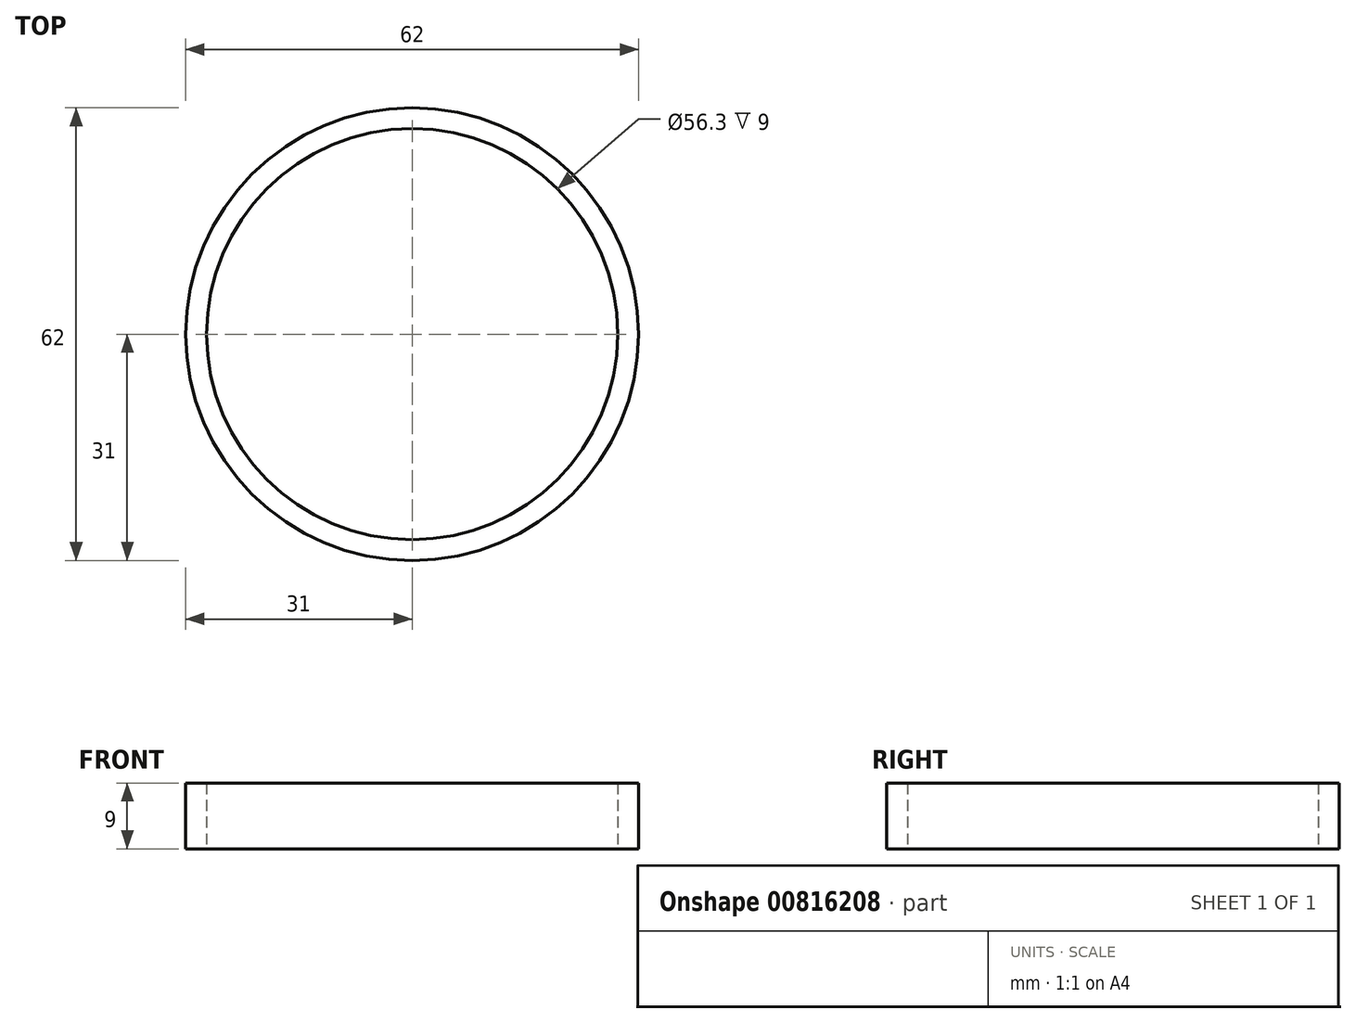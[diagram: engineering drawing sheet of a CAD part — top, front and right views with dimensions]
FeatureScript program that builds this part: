
annotation { "Feature Type Name" : "Feature", "Feature Type Description" : "" }
export const myFeature = defineFeature(function(context is Context, id is Id, definition is map)
    precondition{}
    {
        {
            var Q0;
            Q0=qCreatedBy(makeId("Top.planeOp"),FACE);
            var sketch = newSketch(context, id + "F0", { "sketchPlane" : qUnion([Q0])});
            skCircle(sketch, "E0", {"center": v(0, 0) * mm, "radius": 31 * mm});
            skCircle(sketch, "E1", {"center": v(0, 0) * mm, "radius": 28.15 * mm});
            skSolve(sketch);
        }
        {
            var Q0;
            Q0=makeQuery(id+"F0.imprint","IMPRINT",FACE,{"disambiguationData":[TD([[makeQuery(id+"F0.imprint","IMPRINT",EDGE,{"derivedFrom":sQuery(id+"F0.wireOp",EDGE,"E0")}),1.0]])]});
            var Q1;
            Q1=sQuery(id+"F0.wireOp",EDGE,"E0");
            extrude(context, id + "F1", {"entities" : qUnion([Q0]), "surfaceEntities" : qUnion([Q1]), "depth" : 9 * mm, "offsetDistance" : 25 * mm});
        }
    });
